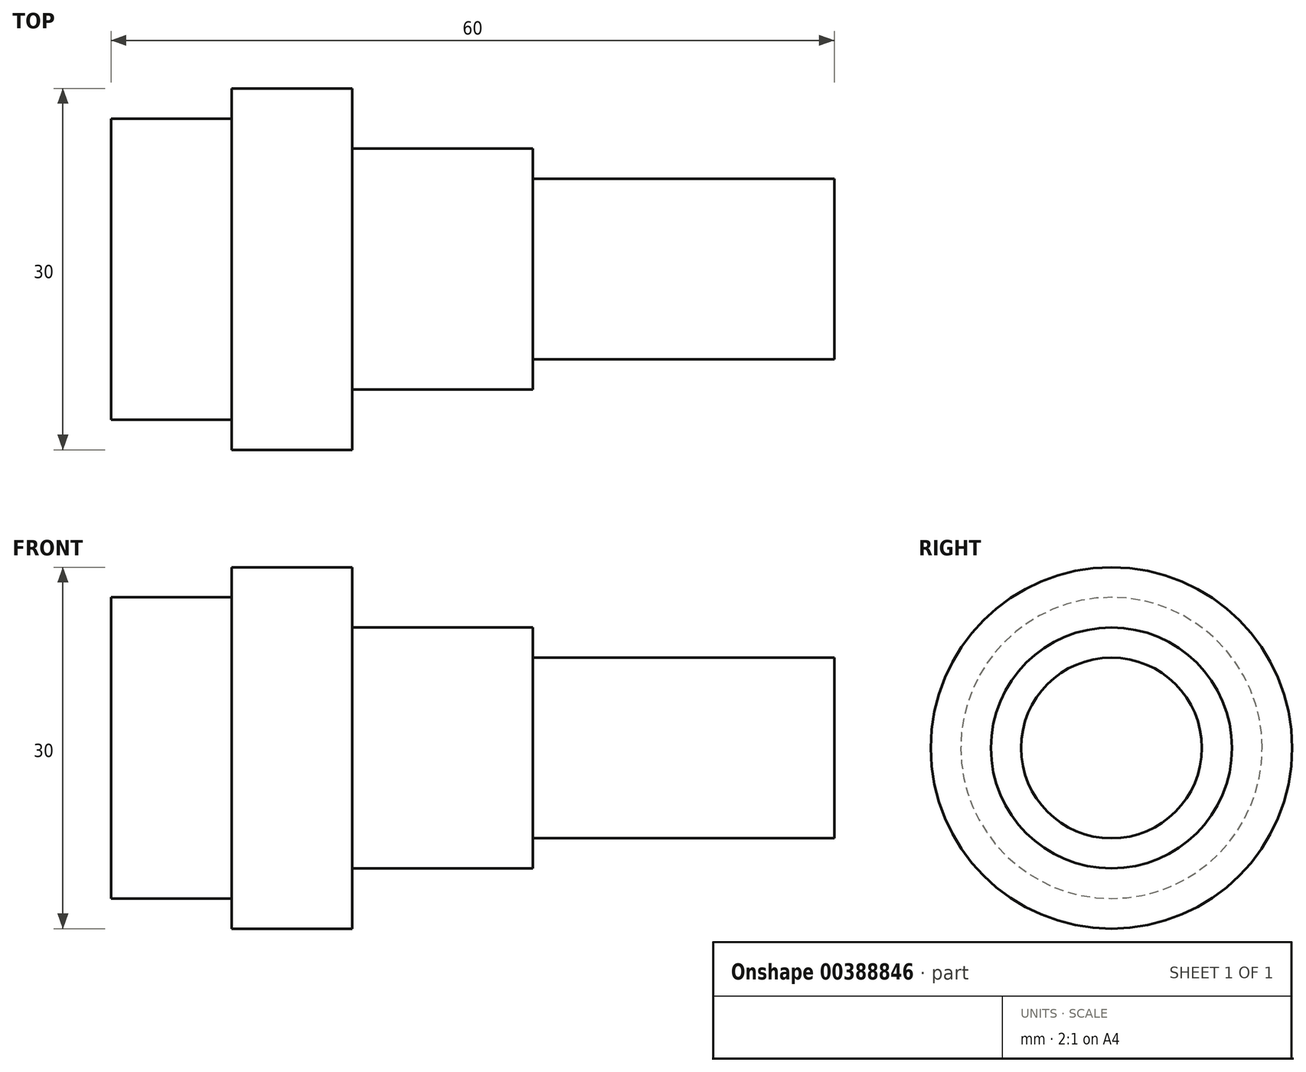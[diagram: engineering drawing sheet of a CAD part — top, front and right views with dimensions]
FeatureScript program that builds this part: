
annotation { "Feature Type Name" : "Feature", "Feature Type Description" : "" }
export const myFeature = defineFeature(function(context is Context, id is Id, definition is map)
    precondition{}
    {
        {
            var Q0;
            Q0=qCreatedBy(makeId("Front.planeOp"),FACE);
            var sketch = newSketch(context, id + "F0", { "sketchPlane" : qUnion([Q0])});
            skLineSegment(sketch, "E0", {"start": v(-60, 0) * mm, "end": v(-60, 12.5) * mm});
            skLineSegment(sketch, "E1", {"start": v(-60, 12.5) * mm, "end": v(-50, 12.5) * mm});
            skLineSegment(sketch, "E2", {"start": v(-50, 12.5) * mm, "end": v(-50, 15) * mm});
            skLineSegment(sketch, "E3", {"start": v(-50, 15) * mm, "end": v(-40, 15) * mm});
            skLineSegment(sketch, "E4", {"start": v(-40, 15) * mm, "end": v(-40, 10) * mm});
            skLineSegment(sketch, "E5", {"start": v(-40, 10) * mm, "end": v(-25, 10) * mm});
            skLineSegment(sketch, "E6", {"start": v(-25, 10) * mm, "end": v(-25, 7.5) * mm});
            skLineSegment(sketch, "E7", {"start": v(-25, 7.5) * mm, "end": v(0, 7.5) * mm});
            skLineSegment(sketch, "E8", {"start": v(0, 7.5) * mm, "end": v(0, 0) * mm});
            skLineSegment(sketch, "E9", {"start": v(-75.1, 0) * mm, "end": v(14.6, 0) * mm, "construction": true});
            skLineSegment(sketch, "E10", {"start": v(-60, 0) * mm, "end": v(0, 0) * mm});
            skSolve(sketch);
        }
        {
            var Q0;
            Q0=makeQuery(id+"F0.imprint","IMPRINT",FACE,{"disambiguationData":[TD([[makeQuery(id+"F0.imprint","IMPRINT",EDGE,{"derivedFrom":sQuery(id+"F0.wireOp",EDGE,"E0")}),-1.0]])]});
            var Q1;
            Q1=sQuery(id+"F0.wireOp",EDGE,"E10");
            revolve(context, id + "F1", {"entities" : qUnion([Q0]), "axis" : qUnion([Q1]), "revolveType" : RevolveType.FULL});
        }
    });
